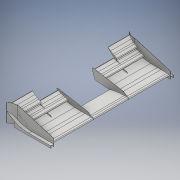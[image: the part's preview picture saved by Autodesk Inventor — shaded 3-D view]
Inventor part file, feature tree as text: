
AUTODESK INVENTOR PART (.ipt)
format: ipt  version: 2018.2 (Build 222227000, 227)  size: 924,672 bytes
history: native  units: mm
features: extrude x16, sketch x16, projected_geometry x12, other x4, chamfer x1, mirror x1
ambient origin geometry x8: Origin, YZ Plane, XZ Plane, XY Plane, X Axis, Y Axis, Z Axis, Center Point
bodies: Body1 (feature_tree)
feature tree (50):
  extrude  "押し出し7"  Depth=394.0mm TaperAngle=0.0deg
  extrude  "押し出し8"  Depth=5.0mm TaperAngle=0.0deg
  extrude  "押し出し9"  Depth=225.0mm TaperAngle=0.0deg
  extrude  "押し出し10"  Depth=5.0mm TaperAngle=0.0deg
  extrude  "押し出し11"  Depth=225.0mm TaperAngle=0.0deg
  extrude  "押し出し13"  Depth=2.0mm
  other  "厚み1"
  other  "厚み2"
  chamfer  "面取り1"  Distance=5.0mm
  extrude  "押し出し16"  Depth=225.0mm TaperAngle=0.0deg
  extrude  "押し出し17"  Depth=1.0mm
  extrude  "押し出し18"  Depth=1.0mm
  extrude  "押し出し20"  Depth=2.0mm
  extrude  "押し出し21"  Depth=2.0mm TaperAngle=45.0deg
  extrude  "押し出し22"  Depth=10.0mm TaperAngle=0.0deg
  extrude  "押し出し23"  Depth=5.0mm
  other  "面を削除1"
  extrude  "押し出し24"  Depth=2.0mm
  extrude  "押し出し25"  TaperAngle=0.0deg  [1 undecoded]
  extrude  "押し出し27"  Depth=35.0mm TaperAngle=0.0deg
  mirror  "ミラー6"
  other  "ソリッド36"
  sketch  "スケッチ8"
  projected_geometry  "投影ループ7"
  sketch  "スケッチ9"
  projected_geometry  "投影ループ8"
  sketch  "スケッチ10"
  projected_geometry  "投影ループ9"
  projected_geometry  "投影ループ10"
  sketch  "スケッチ11"
  projected_geometry  "投影ループ11"
  sketch  "スケッチ12"
  projected_geometry  "投影ループ12"
  projected_geometry  "投影ループ13"
  projected_geometry  "投影ループ14"
  sketch  "スケッチ14"
  projected_geometry  "投影ループ16"
  sketch  "スケッチ18"
  sketch  "スケッチ19"
  sketch  "スケッチ20"
  sketch  "スケッチ21"
  sketch  "スケッチ22"
  sketch  "スケッチ23"
  projected_geometry  "投影ループ18"
  sketch  "スケッチ24"
  projected_geometry  "投影ループ19"
  sketch  "スケッチ25"
  projected_geometry  "投影ループ20"
  sketch  "スケッチ26"
  sketch  "スケッチ27"
note: 1 required parameter value undecoded (feature->parameter linkage not recoverable at this tier; creation-order binding heuristic only, values carry confidence <= 0.55)
